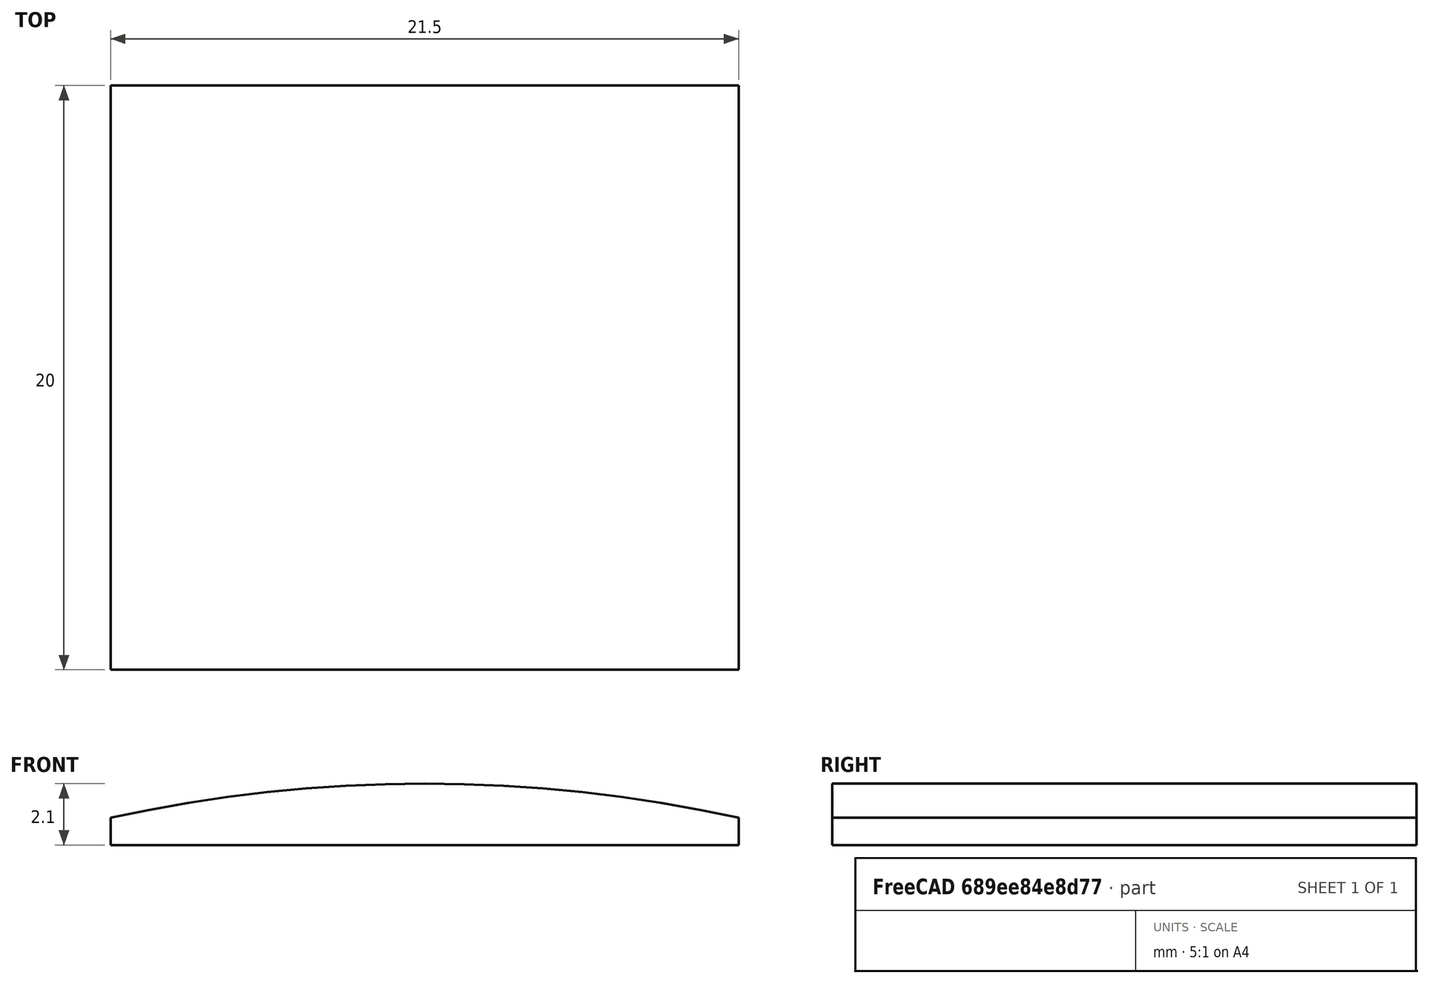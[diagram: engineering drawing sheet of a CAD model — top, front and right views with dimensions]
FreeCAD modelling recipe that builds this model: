
FCSTD DOCUMENT  (FreeCAD 1.0R39109 (Git))
Label: PLASTIC-VSN-DISPLAY-SPACER_1
License: All rights reserved
LicenseURL: https://en.wikipedia.org/wiki/All_rights_reserved
objects: Sketcher::SketchObject×1, PartDesign::Pad×1, PartDesign::Body×1
note: 6 computed .brp shape members not serialized (recipe doc carries the construction recipe); baked Part::Feature solids carry a one-line shape summary decoded from their .brp

FEATURE [Sketcher::SketchObject] Sketch
  ArcFitTolerance = 1e-06
  AttachmentSupport = -> [XZ_Plane]
  FullyConstrained = true
  MakeInternals = false
  MapMode = 5
  Placement = pos=(0,0,0) rot=(1,0,0;1.5708rad)
  sketch-geometry (5):
    g0: LineSegment StartX=-10.75 StartY=0 StartZ=0 EndX=10.75 EndY=0 EndZ=0
    g1: LineSegment StartX=10.75 StartY=0 StartZ=0 EndX=10.75 EndY=0.930702 EndZ=0
    g2: LineSegment StartX=-10.75 StartY=0 StartZ=0 EndX=-10.75 EndY=0.930702 EndZ=0
    g3: ArcOfCircle CenterX=1.03e-14 CenterY=-47.9 CenterZ=0 NormalX=0 NormalY=0 NormalZ=1 AngleXU=0 Radius=50 StartAngle=1.3541 EndAngle=1.78749
    g4: GeomPoint X=0 Y=2.1 Z=0
  constraints (14):
    c: PointOnObject(g0,g-1)
    c: Coincident(g1,g0)
    c: Vertical(g1)
    c: Coincident(g2,g0)
    c: Vertical(g2)
    c: Coincident(g3,g2)
    c: Coincident(g3,g1)
    c: DistanceX(g0,g0) = 21.5
    c: Symmetric(g0,g0,g-1)
    c: PointOnObject(g4,g3)
    c: PointOnObject(g4,g-2)
    c: DistanceY(g-1,g4) = 2.1
    c: Diameter(g3) = 100
    c: Equal(g1,g2)
FEATURE [PartDesign::Pad] Pad
  Direction = (0,-1,2e-16)
  Length = 20
  Length2 = 10
  Midplane = true
  Placement = pos=(0,0,0) rot=(1,0,0;1.5708rad)
  Profile = -> Sketch
  ReferenceAxis = -> Sketch [N_Axis]
  Refine = true
  Suppressed = false
  Type = 0
FEATURE [PartDesign::Body] Body
  AllowCompound = false
  Group = -> [Sketch,Pad]
  Origin = -> Origin
  Tip = -> Pad
